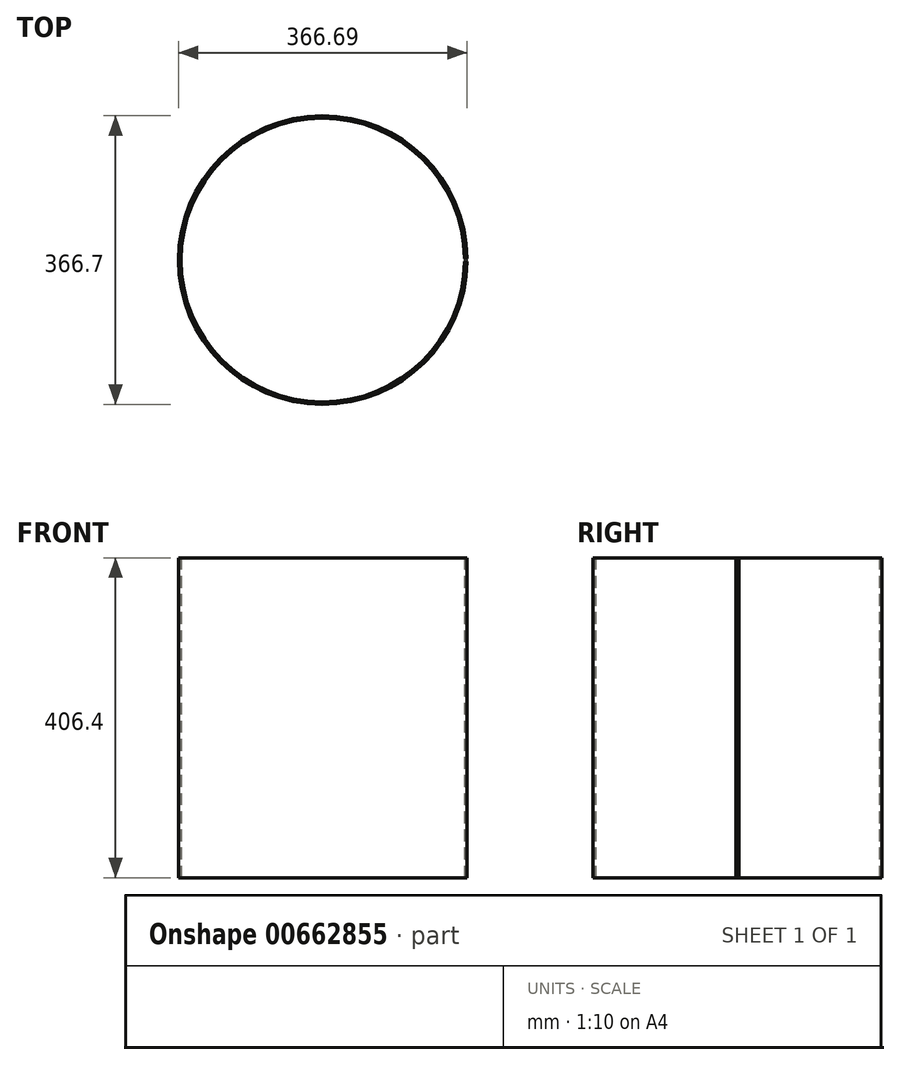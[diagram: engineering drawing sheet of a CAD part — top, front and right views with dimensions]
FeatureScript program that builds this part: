
annotation { "Feature Type Name" : "Feature", "Feature Type Description" : "" }
export const myFeature = defineFeature(function(context is Context, id is Id, definition is map)
    precondition{}
    {
        {
            var Q0;
            Q0=qCreatedBy(makeId("Top.planeOp"),FACE);
            var sketch = newSketch(context, id + "F0", { "sketchPlane" : qUnion([Q0])});
            skCircle(sketch, "E0", {"center": v(0, 0) * mm, "radius": 181.76 * mm, "construction": true});
            skPoint(sketch, "E1", {"position": v(181.76, 0) * mm});
            skCircle(sketch, "E2.0", {"center": v(0, 0) * mm, "radius": 183.35 * mm});
            skCircle(sketch, "E3.0", {"center": v(0, 0) * mm, "radius": 180.17 * mm});
            skLineSegment(sketch, "E4", {"start": v(180.17, 0) * mm, "end": v(183.35, 0) * mm});
            skSolve(sketch);
        }
        {
            var Q0;
            Q0=makeQuery(id+"F0.imprint","IMPRINT",FACE,{"disambiguationData":[TD([[makeQuery(id+"F0.imprint","IMPRINT",EDGE,{"derivedFrom":sQuery(id+"F0.wireOp",EDGE,"E2.0")}),1.0]])]});
            extrude(context, id + "F1", {"entities" : qUnion([Q0]), "depth" : 406.4 * mm, "offsetDistance" : 25.4 * mm});
        }
        {
            var Q0;
            Q0=qCreatedBy(makeId("Top.planeOp"),FACE);
            var sketch = newSketch(context, id + "F2", { "sketchPlane" : qUnion([Q0])});
            skLineSegment(sketch, "E5", {"start": v(0, 0) * mm, "end": v(222.6, 0) * mm, "construction": true});
            skLineSegment(sketch, "E6.0", {"start": v(0, -0.4) * mm, "end": v(222.6, -0.4) * mm});
            skLineSegment(sketch, "E7.0", {"start": v(0, 0.4) * mm, "end": v(222.6, 0.4) * mm});
            skLineSegment(sketch, "E8", {"start": v(0, -0.4) * mm, "end": v(0, 0.4) * mm});
            skLineSegment(sketch, "E9", {"start": v(222.6, 0.4) * mm, "end": v(222.6, -0.4) * mm});
            skSolve(sketch);
        }
        {
            var Q0;
            Q0=makeQuery(id+"F2.imprint","IMPRINT",FACE,{"disambiguationData":[TD([[makeQuery(id+"F2.imprint","IMPRINT",EDGE,{"derivedFrom":sQuery(id+"F2.wireOp",EDGE,"E6.0")}),1.0]])]});
            extrude(context, id + "F3", {"entities" : qUnion([Q0]), "depth" : 406.4 * mm, "offsetDistance" : 25.4 * mm});
        }
        {
            var Q0;
            Q0=makeQuery(id+"F3.opExtrude","SWEPT_BODY",BODY,{"disambiguationData":[OSD([sQuery(id+"F2.wireOp",EDGE,"E6.0"),sQuery(id+"F2.wireOp",EDGE,"E7.0"),sQuery(id+"F2.wireOp",EDGE,"E8"),sQuery(id+"F2.wireOp",EDGE,"E9")])]});
            var Q1;
            Q1=makeQuery(id+"F1.opExtrude","SWEPT_BODY",BODY,{"disambiguationData":[OSD([sQuery(id+"F0.wireOp",EDGE,"E2.0"),sQuery(id+"F0.wireOp",EDGE,"E3.0")])]});
            booleanBodies(context, id + "F4", {"operationType" : BooleanOperationType.SUBTRACTION, "tools" : qUnion([Q0]), "targets" : qUnion([Q1])});
        }
        {
            var Q0;
            Q0=makeQuery(id+"F4.opBoolean","INTERSECT",EDGE,{"derivedFrom":[makeQuery(id+"F1.opExtrude","SWEPT_FACE",FACE,{"disambiguationData":[OSD([sQuery(id+"F0.wireOp",EDGE,"E2.0")])]}),makeQuery(id+"F3.opExtrude","SWEPT_FACE",FACE,{"disambiguationData":[OSD([sQuery(id+"F2.wireOp",EDGE,"E7.0")])]})]});
            chamfer(context, id + "F5", {"entities" : qUnion([Q0]), "chamferType" : ChamferType.OFFSET_ANGLE, "width" : 1.59 * mm, "oppositeDirection" : false, "angle" : 45 * degree, "tangentPropagation" : true});
        }
        {
            var Q0;
            Q0=makeQuery(id+"F4.opBoolean","INTERSECT",EDGE,{"derivedFrom":[makeQuery(id+"F1.opExtrude","SWEPT_FACE",FACE,{"disambiguationData":[OSD([sQuery(id+"F0.wireOp",EDGE,"E3.0")])]}),makeQuery(id+"F3.opExtrude","SWEPT_FACE",FACE,{"disambiguationData":[OSD([sQuery(id+"F2.wireOp",EDGE,"E7.0")])]})]});
            chamfer(context, id + "F6", {"entities" : qUnion([Q0]), "width" : 1.59 * mm, "tangentPropagation" : true});
        }
        {
            var Q0;
            Q0=makeQuery(id+"F4.opBoolean","INTERSECT",EDGE,{"derivedFrom":[makeQuery(id+"F1.opExtrude","SWEPT_FACE",FACE,{"disambiguationData":[OSD([sQuery(id+"F0.wireOp",EDGE,"E2.0")])]}),makeQuery(id+"F3.opExtrude","SWEPT_FACE",FACE,{"disambiguationData":[OSD([sQuery(id+"F2.wireOp",EDGE,"E6.0")])]})]});
            chamfer(context, id + "F7", {"entities" : qUnion([Q0]), "width" : 1.59 * mm, "tangentPropagation" : true});
        }
        {
            var Q0;
            Q0=makeQuery(id+"F4.opBoolean","INTERSECT",EDGE,{"derivedFrom":[makeQuery(id+"F1.opExtrude","SWEPT_FACE",FACE,{"disambiguationData":[OSD([sQuery(id+"F0.wireOp",EDGE,"E3.0")])]}),makeQuery(id+"F3.opExtrude","SWEPT_FACE",FACE,{"disambiguationData":[OSD([sQuery(id+"F2.wireOp",EDGE,"E6.0")])]})]});
            chamfer(context, id + "F8", {"entities" : qUnion([Q0]), "width" : 1.59 * mm, "tangentPropagation" : true});
        }
    });
